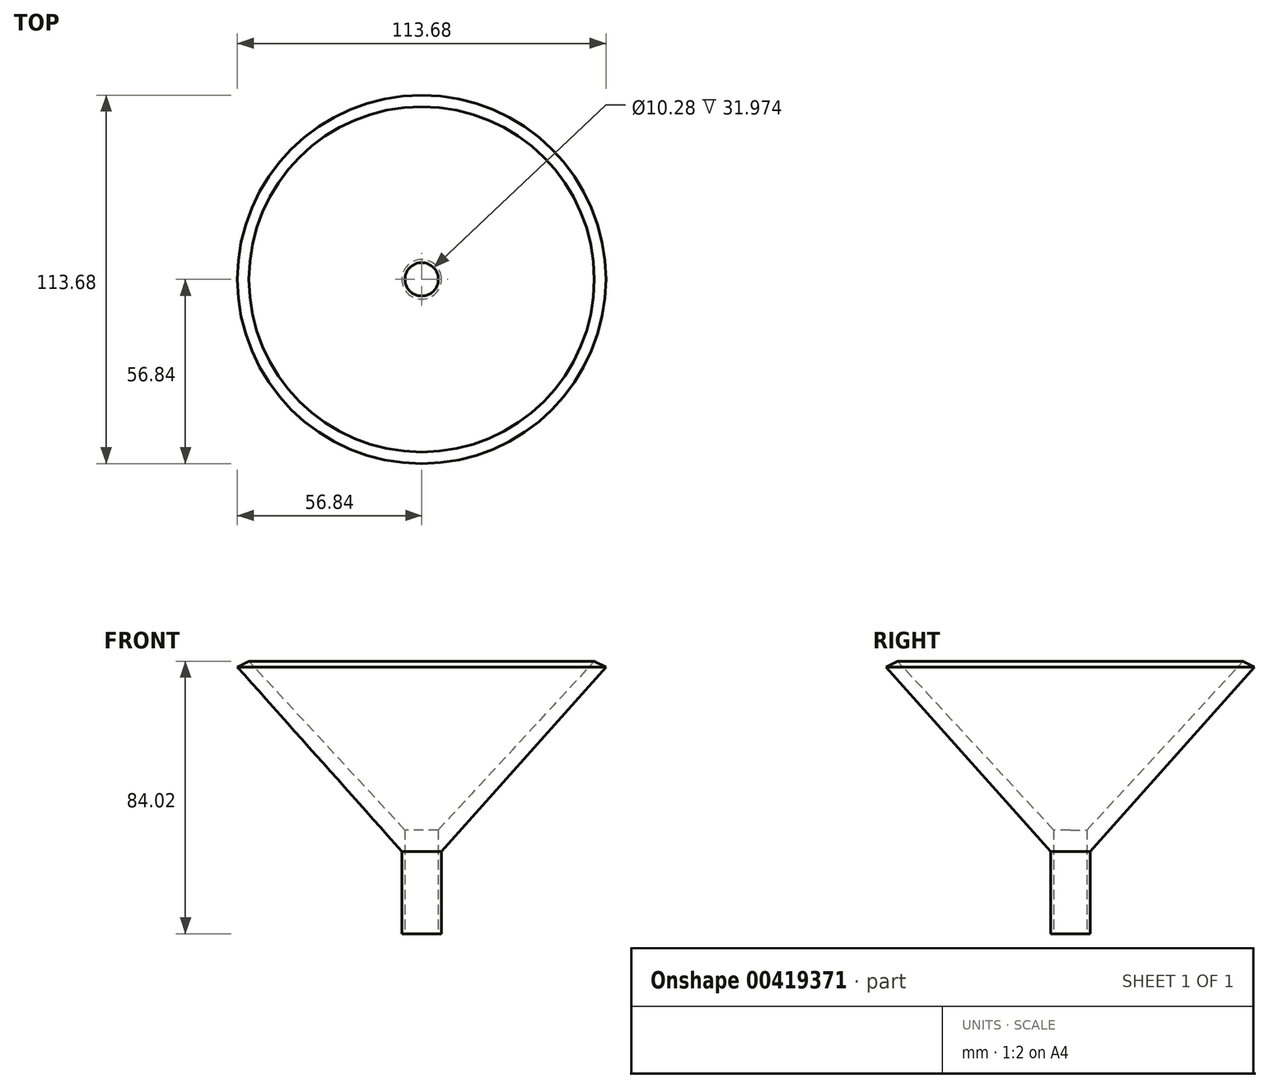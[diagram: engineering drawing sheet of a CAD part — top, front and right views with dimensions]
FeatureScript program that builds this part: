
annotation { "Feature Type Name" : "Feature", "Feature Type Description" : "" }
export const myFeature = defineFeature(function(context is Context, id is Id, definition is map)
    precondition{}
    {
        {
            var Q0;
            Q0=qCreatedBy(makeId("Front.planeOp"),FACE);
            var sketch = newSketch(context, id + "F0", { "sketchPlane" : qUnion([Q0])});
            skLineSegment(sketch, "E0", {"start": v(50.73, 56.86) * mm, "end": v(0, 0) * mm});
            skLineSegment(sketch, "E1", {"start": v(0, 0) * mm, "end": v(0, -25.4) * mm});
            skLineSegment(sketch, "E2", {"start": v(0, -25.4) * mm, "end": v(-6.11, -25.4) * mm});
            skLineSegment(sketch, "E3", {"start": v(-6.11, -25.4) * mm, "end": v(-6.11, 1.01) * mm});
            skLineSegment(sketch, "E4", {"start": v(-6.11, 1.01) * mm, "end": v(47.17, 58.62) * mm});
            skLineSegment(sketch, "E5", {"start": v(47.17, 58.62) * mm, "end": v(50.73, 56.86) * mm});
            skSolve(sketch);
        }
        {
            var Q0;
            Q0=makeQuery(id+"F0.imprint","IMPRINT",FACE,{"disambiguationData":[TD([[makeQuery(id+"F0.imprint","IMPRINT",EDGE,{"derivedFrom":sQuery(id+"F0.wireOp",EDGE,"E0")}),-1.0]])]});
            var Q1;
            Q1=sQuery(id+"F0.wireOp",EDGE,"E3");
            revolve(context, id + "F1", {"entities" : qUnion([Q0]), "axis" : qUnion([Q1]), "revolveType" : RevolveType.FULL});
        }
        {
            var Q0;
            Q0=makeQuery(id+"F1.opRevolve","SWEPT_FACE",FACE,{"disambiguationData":[OSD([sQuery(id+"F0.wireOp",EDGE,"E2")])]});
            var sketch = newSketch(context, id + "F2", { "sketchPlane" : qUnion([Q0])});
            skCircle(sketch, "E6", {"center": v(-6.11, 0) * mm, "radius": 5.14 * mm});
            skSolve(sketch);
        }
        {
            var Q0;
            Q0 = qSketchRegion(id + "F2", true);
            extrude(context, id + "F3", {"entities" : qUnion([Q0]), "operationType" : NewBodyOperationType.REMOVE, "oppositeDirection" : true, "depth" : 50.8 * mm});
        }
    });
